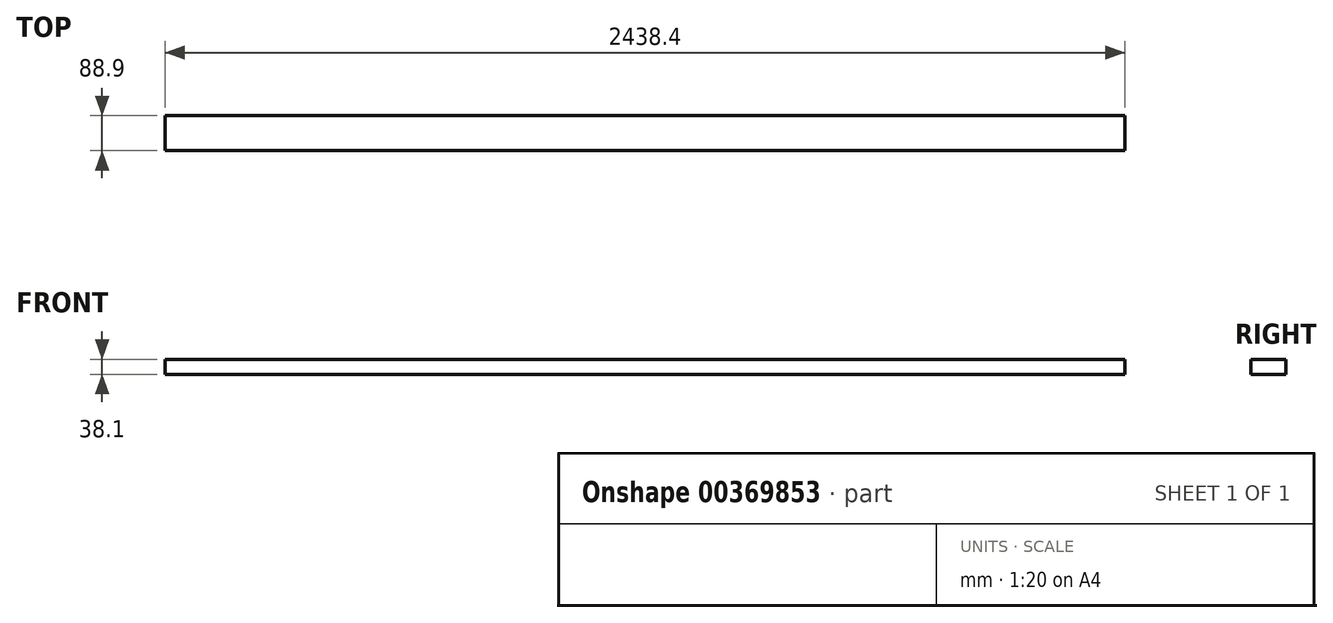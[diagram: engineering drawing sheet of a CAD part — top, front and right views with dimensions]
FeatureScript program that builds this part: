
annotation { "Feature Type Name" : "Feature", "Feature Type Description" : "" }
export const myFeature = defineFeature(function(context is Context, id is Id, definition is map)
    precondition{}
    {
        {
            var Q0;
            Q0=qCreatedBy(makeId("Top.planeOp"),FACE);
            var sketch = newSketch(context, id + "F0", { "sketchPlane" : qUnion([Q0])});
            skLineSegment(sketch, "E0.bottom", {"start": v(1219.2, -44.45) * mm, "end": v(-1219.2, -44.45) * mm});
            skLineSegment(sketch, "E0.top", {"start": v(1219.2, 44.45) * mm, "end": v(-1219.2, 44.45) * mm});
            skLineSegment(sketch, "E0.left", {"start": v(1219.2, -44.45) * mm, "end": v(1219.2, 44.45) * mm});
            skLineSegment(sketch, "E0.right", {"start": v(-1219.2, -44.45) * mm, "end": v(-1219.2, 44.45) * mm});
            skPoint(sketch, "E0.middle", {"position": v(0, 0) * mm});
            skSolve(sketch);
        }
        {
            var Q0;
            Q0 = qSketchRegion(id + "F0", true);
            extrude(context, id + "F1", {"entities" : qUnion([Q0]), "oppositeDirection" : true, "depth" : 38.1 * mm});
        }
    });
